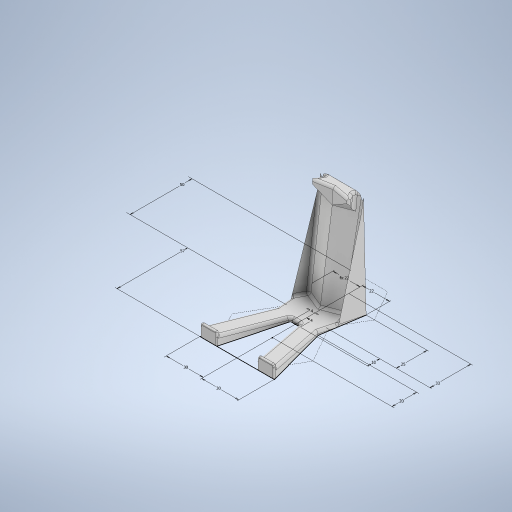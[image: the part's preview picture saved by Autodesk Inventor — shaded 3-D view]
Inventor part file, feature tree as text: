
AUTODESK INVENTOR PART (.ipt)
format: ipt  version: 2023 (Build 270158030, 158C)  size: 605,184 bytes
history: native  units: mm
features: sketch x5, extrude x5, fillet x5, projected_geometry x5, chamfer x1
ambient origin geometry x8: Origin, YZ Plane, XZ Plane, XY Plane, X Axis, Y Axis, Z Axis, Center Point
bodies: Body1 (feature_tree)
feature tree (21):
  sketch  "Sketch2"  dims[d4=57.0mm d5=50.0mm]
  extrude  "Extrusion2"  Depth=50.0mm
  extrude  "Extrusion3"  Depth=30.0mm
  extrude  "Extrusion4"  Depth=10.0mm
  extrude  "Extrusion5"  Depth=20.0mm
  fillet  "Fillet1"  Radius=25.0mm
  fillet  "Fillet2"  Radius=33.0mm
  fillet  "Fillet3"  Radius=22.0mm
  fillet  "Fillet4"  Radius=22.0mm
  extrude  "Extrusion6"  Depth=2.0mm
  chamfer  "Chamfer1"  Distance=2.0mm
  fillet  "Fillet5"  [1 undecoded]
  sketch  "Sketch4"  dims[d6=30.0mm d7=30.0mm]
  projected_geometry  "Projected Loop1"
  projected_geometry  "Projected Loop2"
  projected_geometry  "Projected Loop3"
  sketch  "Sketch5"  dims[d8=10.0mm d9=4.0mm]
  sketch  "Sketch6"  dims[d10=4.0mm d11=20.0mm d12=25.0mm d13=33.0mm d14=22.0mm d15=22.0mm]
  projected_geometry  "Projected Loop4"
  sketch  "Sketch7"  dims[d16=10.0mm d17=0.0mm d18=0.872665mm d20=2.0mm d21=0.0mm d22=3.0mm d23=3.0mm d24=0.0mm d25=0.0mm d26=6.0mm d27=6.0mm d28=15.0mm d29=80.0mm d30=-0.523599mm d31=13.0mm d32=6.0mm d33=80.0mm d34=-0.349066mm d35=2.0mm d36=2.0mm d37=1.0mm d38=5.0mm d39=10.0mm d40=10.0mm d42=10.0mm d43=3.0mm d44=0.0mm d45=2.0mm d46=2.0mm d47=1.0mm d48=9.4mm d49=2.0mm d50=45.0deg d51=2.0mm]
  projected_geometry  "Projected Loop5"
note: 1 required parameter value undecoded (feature->parameter linkage not recoverable at this tier; creation-order binding heuristic only, values carry confidence <= 0.55)
